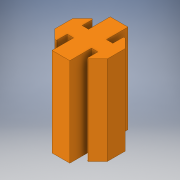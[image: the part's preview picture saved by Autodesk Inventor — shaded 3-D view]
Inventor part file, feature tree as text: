
AUTODESK INVENTOR PART (.ipt)
format: ipt  version: 2019 (Build 230136000, 136)  size: 140,800 bytes
history: native  units: in
note: dims shown in document units (in); Inventor stores cm internally (conversion verified against a paired STEP export)
features: extrude x1, fillet x1, sketch x1
ambient origin geometry x8: Origin, YZ Plane, XZ Plane, XY Plane, X Axis, Y Axis, Z Axis, Center Point
bodies: Body1 (feature_tree)
feature tree (3):
  extrude  "Extrusion2"  Depth=0.655in
  fillet  "Fillet1"  Radius=0.073in
  sketch  "Sketch1"  dims[d0=0.2in d1=0.655in d2=0.073in d4=0.1677in d9=0.121in d12=0.0in d15=0.442in d16=0.442in d20=135.0deg d21=135.0deg d24=0.2437in d25=0.655in d26=0.1372in d33=0.1372in d34=0.121in d35=0.073in d36=0.2437in d37=0.2in d38=0.2in d39=135.0deg d40=135.0deg d41=1.0in d42=0.0in d43=0.01in]
